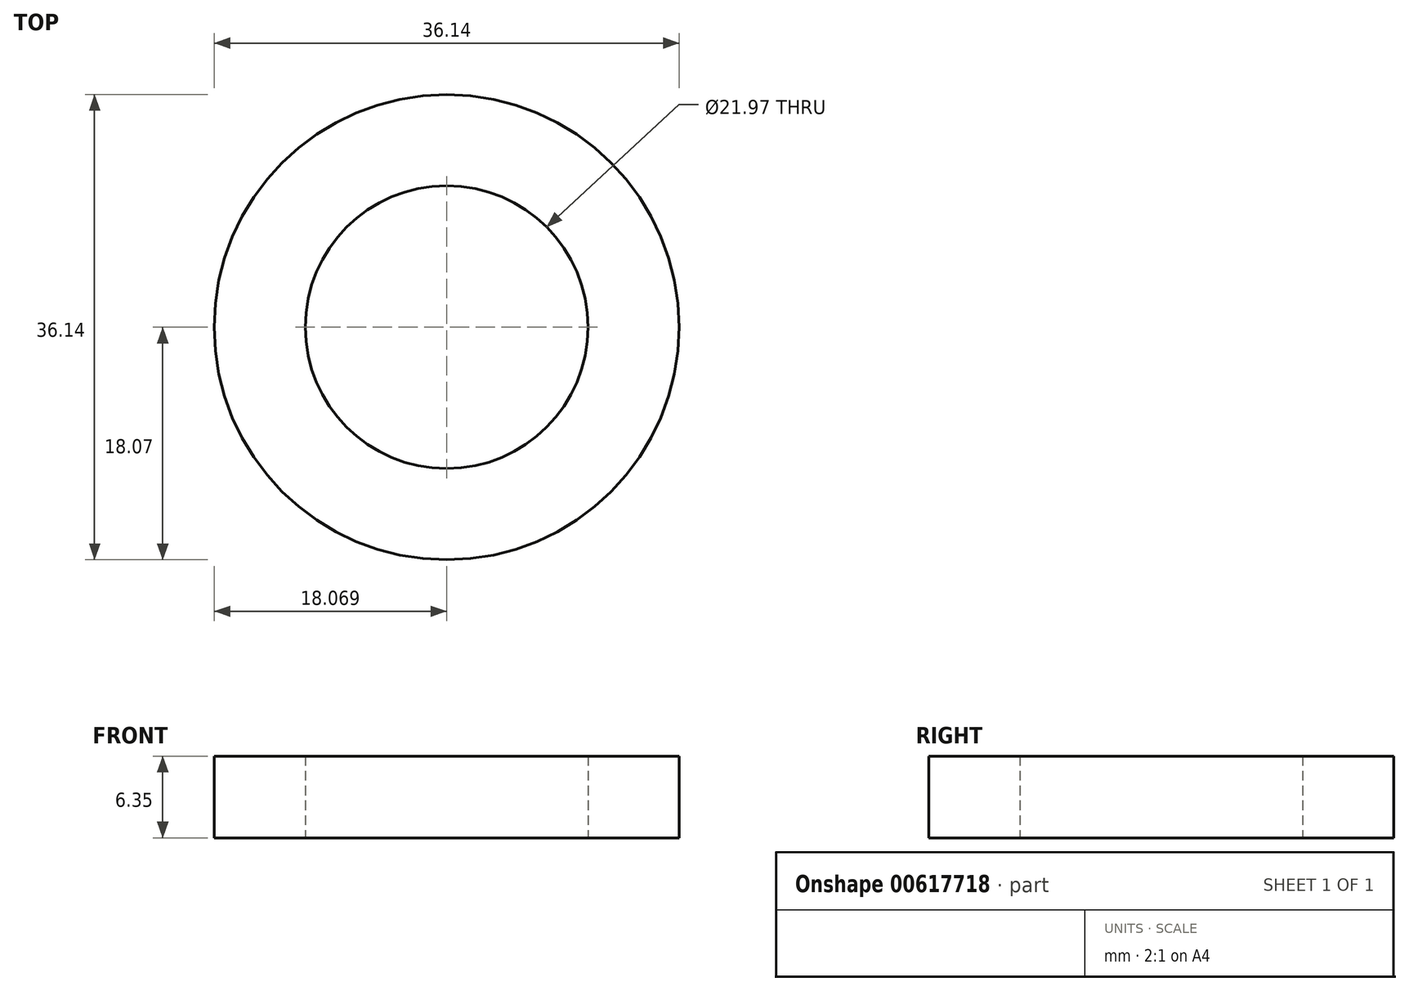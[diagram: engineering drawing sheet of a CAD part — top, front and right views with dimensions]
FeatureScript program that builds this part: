
annotation { "Feature Type Name" : "Feature", "Feature Type Description" : "" }
export const myFeature = defineFeature(function(context is Context, id is Id, definition is map)
    precondition{}
    {
        {
            var Q0;
            Q0=qCreatedBy(makeId("Top.planeOp"),FACE);
            var sketch = newSketch(context, id + "F0", { "sketchPlane" : qUnion([Q0])});
            skCircle(sketch, "E0", {"center": v(-19.5, 32.16) * mm, "radius": 18.07 * mm});
            skCircle(sketch, "E1", {"center": v(37.08, 0) * mm, "radius": 18.07 * mm});
            skCircle(sketch, "E2", {"center": v(0, 0) * mm, "radius": 18.07 * mm});
            skCircle(sketch, "E3", {"center": v(-18.45, -32.16) * mm, "radius": 18.07 * mm});
            skArc(sketch, "E4", {"start": v(-22.18, -14.48) * mm, "mid": v(-18.66, -0.25) * mm, "end": v(-21.25, 14.18) * mm});
            skArc(sketch, "E5", {"start": v(-2.43, 26.26) * mm, "mid": v(8.77, 16.4) * mm, "end": v(22.6, 10.8) * mm});
            skArc(sketch, "E6", {"start": v(23.2, -11.56) * mm, "mid": v(9.24, -15.74) * mm, "end": v(-1.72, -25.33) * mm});
            skCircle(sketch, "E7", {"center": v(-19.5, 32.16) * mm, "radius": 10.99 * mm});
            skCircle(sketch, "E8", {"center": v(37.08, 0) * mm, "radius": 10.99 * mm});
            skCircle(sketch, "E9", {"center": v(-18.45, -32.16) * mm, "radius": 10.99 * mm});
            skCircle(sketch, "E10", {"center": v(0, 0) * mm, "radius": 10.99 * mm});
            skSolve(sketch);
        }
        {
            var Q0;
            Q0=makeQuery(id+"F0.imprint","IMPRINT",FACE,{"disambiguationData":[TD([[makeQuery(id+"F0.imprint","IMPRINT",EDGE,{"derivedFrom":sQuery(id+"F0.wireOp",EDGE,"E8")}),-1.0]])]});
            extrude(context, id + "F1", {"entities" : qUnion([Q0]), "depth" : 6.35 * mm, "offsetDistance" : 25.4 * mm});
        }
    });
